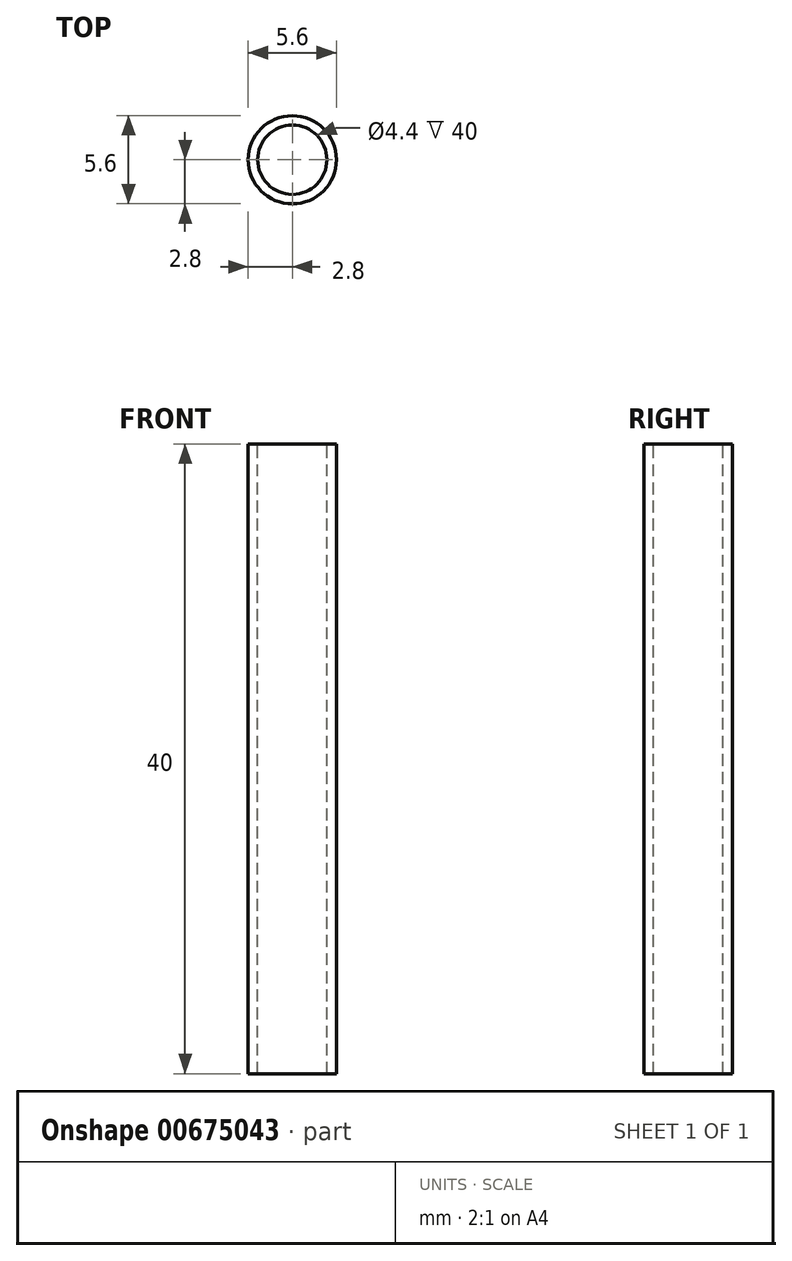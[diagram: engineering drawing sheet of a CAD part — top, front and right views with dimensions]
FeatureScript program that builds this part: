
annotation { "Feature Type Name" : "Feature", "Feature Type Description" : "" }
export const myFeature = defineFeature(function(context is Context, id is Id, definition is map)
    precondition{}
    {
        {
            var Q0;
            Q0=qCreatedBy(makeId("Top.planeOp"),FACE);
            var sketch = newSketch(context, id + "F0", { "sketchPlane" : qUnion([Q0])});
            skCircle(sketch, "E0", {"center": v(0, 0) * mm, "radius": 2.8 * mm});
            skSolve(sketch);
        }
        {
            var Q0;
            Q0 = qSketchRegion(id + "F0", true);
            extrude(context, id + "F1", {"entities" : qUnion([Q0]), "depth" : 40 * mm, "offsetDistance" : 25 * mm});
        }
        {
            var Q0;
            Q0=makeQuery(id+"F1.opExtrude","CAP_FACE",FACE,{"disambiguationData":[OSD([sQuery(id+"F0.wireOp",EDGE,"E0")])],"isStart":false});
            var sketch = newSketch(context, id + "F2", { "sketchPlane" : qUnion([Q0])});
            skPoint(sketch, "E1", {"position": v(0, 0) * mm});
            skSolve(sketch);
        }
        {
            var Q0;
            Q0=sQuery(id+"F2.wireOp",VERTEX,"E1");
            var Q1;
            Q1=makeQuery(id+"F1.opExtrude","SWEPT_BODY",BODY,{"disambiguationData":[OSD([sQuery(id+"F0.wireOp",EDGE,"E0")])]});
            hole(context, id + "F3", {"style" : HoleStyle.SIMPLE, "endStyle" : HoleEndStyle.THROUGH, "holeDiameter" : 4.4 * mm, "majorDiameter" : 5 * mm, "isTappedThrough" : true, "tappedDepth" : 12 * mm, "tapClearance" : 3, "locations" : qUnion([Q0]), "scope" : qUnion([Q1])});
        }
    });
